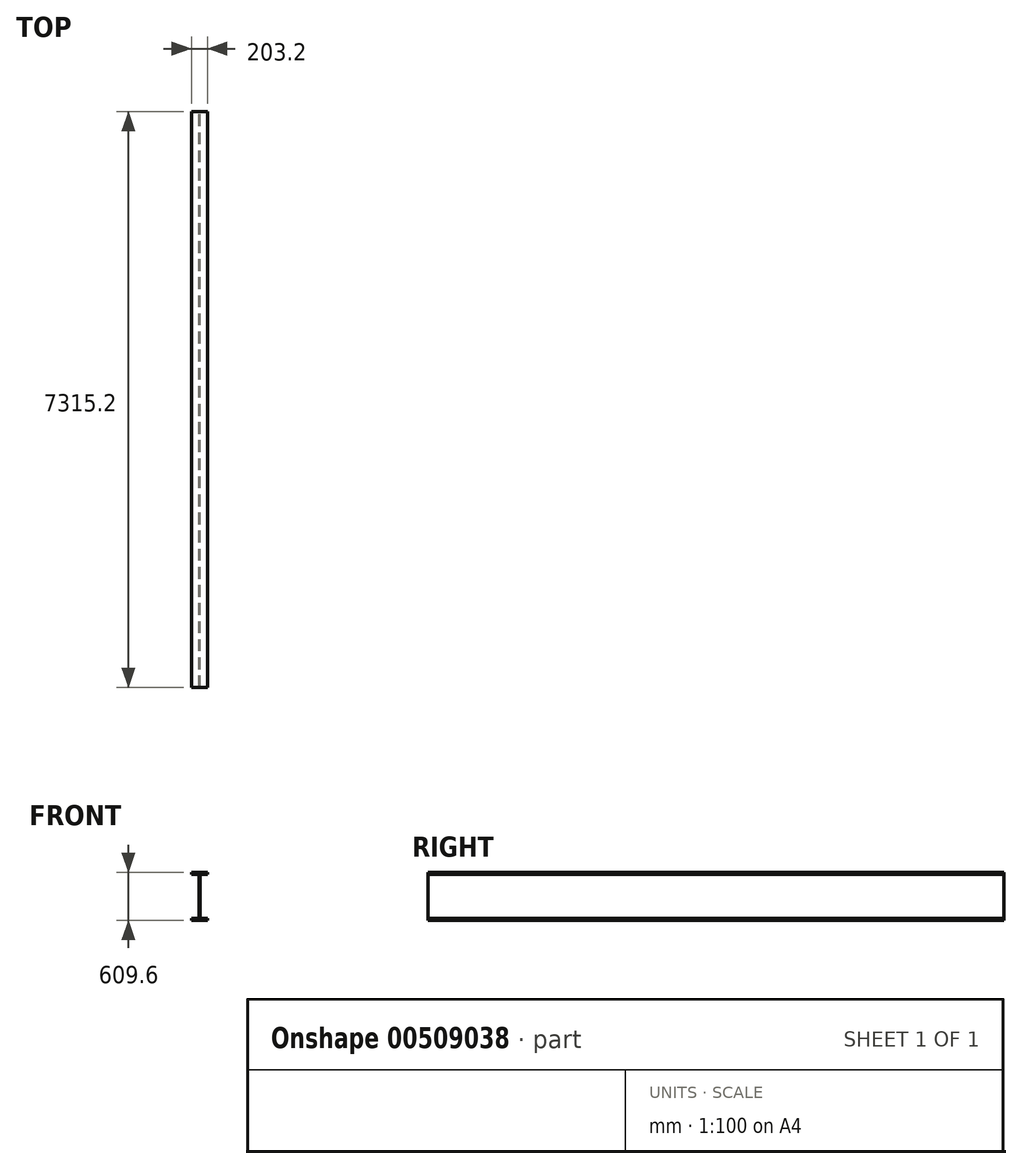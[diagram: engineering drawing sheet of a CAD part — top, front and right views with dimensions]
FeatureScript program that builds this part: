
annotation { "Feature Type Name" : "Feature", "Feature Type Description" : "" }
export const myFeature = defineFeature(function(context is Context, id is Id, definition is map)
    precondition{}
    {
        {
            var Q0;
            Q0=qCreatedBy(makeId("Front.planeOp"),FACE);
            var sketch = newSketch(context, id + "F0", { "sketchPlane" : qUnion([Q0])});
            skLineSegment(sketch, "E0", {"start": v(101.6, -279.4) * mm, "end": v(8.89, -279.4) * mm});
            skLineSegment(sketch, "E1", {"start": v(6.35, -276.86) * mm, "end": v(6.35, 276.86) * mm});
            skLineSegment(sketch, "E2", {"start": v(8.89, 279.4) * mm, "end": v(101.6, 279.4) * mm});
            skLineSegment(sketch, "E3", {"start": v(-101.6, 279.4) * mm, "end": v(-8.89, 279.4) * mm});
            skLineSegment(sketch, "E4", {"start": v(-6.35, 276.86) * mm, "end": v(-6.35, -276.86) * mm});
            skLineSegment(sketch, "E5", {"start": v(-8.89, -279.4) * mm, "end": v(-101.6, -279.4) * mm});
            skLineSegment(sketch, "E6", {"start": v(0, 0) * mm, "end": v(-6.35, 0) * mm, "construction": true});
            skLineSegment(sketch, "E7", {"start": v(0, 0) * mm, "end": v(6.35, 0) * mm, "construction": true});
            skLineSegment(sketch, "E8", {"start": v(0, 0) * mm, "end": v(0, 304.8) * mm, "construction": true});
            skLineSegment(sketch, "E9", {"start": v(0, 0) * mm, "end": v(0, -304.8) * mm, "construction": true});
            skPoint(sketch, "E10.visualSharp", {"position": v(-6.35, 279.4) * mm});
            skArc(sketch, "E10.filletArc", {"start": v(-6.35, 276.86) * mm, "mid": v(-7.1, 278.66) * mm, "end": v(-8.89, 279.4) * mm});
            skPoint(sketch, "E11.visualSharp", {"position": v(6.35, 279.4) * mm});
            skArc(sketch, "E11.filletArc", {"start": v(8.89, 279.4) * mm, "mid": v(7.1, 278.66) * mm, "end": v(6.35, 276.86) * mm});
            skPoint(sketch, "E12.visualSharp", {"position": v(6.35, -279.4) * mm});
            skArc(sketch, "E12.filletArc", {"start": v(6.35, -276.86) * mm, "mid": v(7.1, -278.66) * mm, "end": v(8.89, -279.4) * mm});
            skPoint(sketch, "E13.visualSharp", {"position": v(-6.35, -279.4) * mm});
            skArc(sketch, "E13.filletArc", {"start": v(-8.89, -279.4) * mm, "mid": v(-7.1, -278.66) * mm, "end": v(-6.35, -276.86) * mm});
            skPoint(sketch, "E14.visualSharp", {"position": v(-101.6, 304.8) * mm});
            skPoint(sketch, "E15.visualSharp", {"position": v(101.6, 304.8) * mm});
            skPoint(sketch, "E16.visualSharp", {"position": v(101.6, 279.4) * mm});
            skPoint(sketch, "E17.visualSharp", {"position": v(101.6, -304.8) * mm});
            skPoint(sketch, "E18.visualSharp", {"position": v(-101.6, -279.4) * mm});
            skPoint(sketch, "E19.visualSharp", {"position": v(-101.6, -304.8) * mm});
            skLineSegment(sketch, "E20", {"start": v(101.6, -279.4) * mm, "end": v(101.6, -304.8) * mm});
            skLineSegment(sketch, "E21", {"start": v(-101.6, -279.4) * mm, "end": v(-101.6, -304.8) * mm});
            skLineSegment(sketch, "E22", {"start": v(-101.6, 304.8) * mm, "end": v(-101.6, 279.4) * mm});
            skLineSegment(sketch, "E23", {"start": v(101.6, 304.8) * mm, "end": v(101.6, 279.4) * mm});
            skLineSegment(sketch, "E24", {"start": v(-101.6, 304.8) * mm, "end": v(101.6, 304.8) * mm});
            skLineSegment(sketch, "E25", {"start": v(-101.6, -304.8) * mm, "end": v(101.6, -304.8) * mm});
            skSolve(sketch);
        }
        {
            var Q0;
            Q0=makeQuery(id+"F0.imprint","IMPRINT",FACE,{"disambiguationData":[TD([[makeQuery(id+"F0.imprint","IMPRINT",EDGE,{"derivedFrom":sQuery(id+"F0.wireOp",EDGE,"E0")}),1.0]])]});
            extrude(context, id + "F1", {"entities" : qUnion([Q0]), "depth" : 7315.2 * mm});
        }
    });
